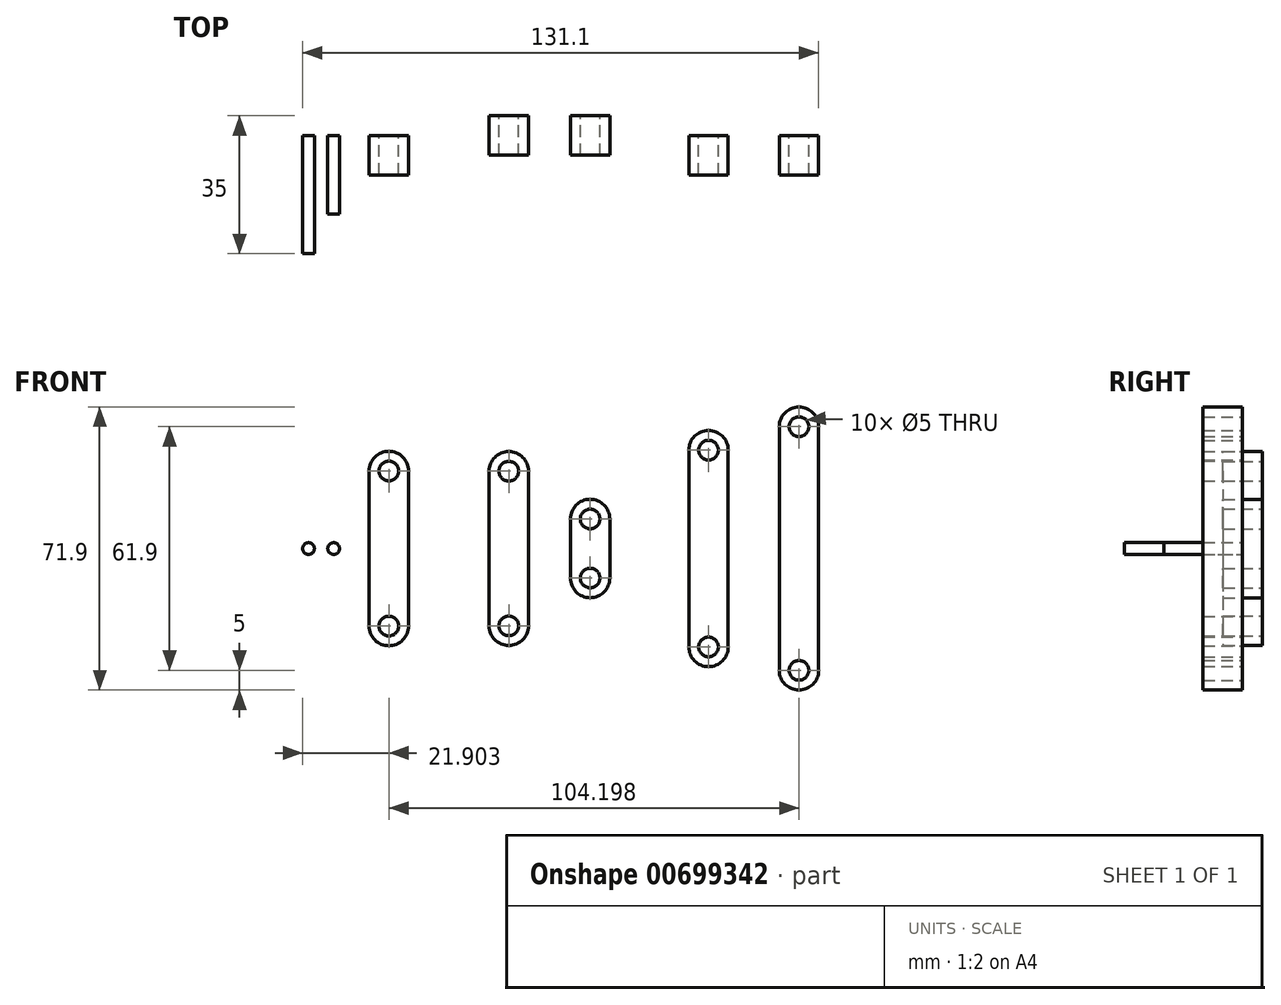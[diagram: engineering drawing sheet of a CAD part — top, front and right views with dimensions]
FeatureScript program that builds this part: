
annotation { "Feature Type Name" : "Feature", "Feature Type Description" : "" }
export const myFeature = defineFeature(function(context is Context, id is Id, definition is map)
    precondition{}
    {
        {
            assignVariable(context, id + "F0", {"name" : "thinkness", "anyValue" : 10});
        }
        {
            var Q0;
            Q0=qCreatedBy(makeId("Front.planeOp"),FACE);
            var sketch = newSketch(context, id + "F1", { "sketchPlane" : qUnion([Q0])});
            skCircle(sketch, "E0", {"center": v(0, 7.5) * mm, "radius": 2.5 * mm});
            skArc(sketch, "E1", {"start": v(5, 7.5) * mm, "mid": v(0, 12.5) * mm, "end": v(-5, 7.5) * mm});
            skLineSegment(sketch, "E2", {"start": v(-5, 7.5) * mm, "end": v(-5, 0) * mm});
            skLineSegment(sketch, "E3", {"start": v(-5, 0) * mm, "end": v(5, 0) * mm, "construction": true});
            skLineSegment(sketch, "E4", {"start": v(5, 0) * mm, "end": v(5, 7.5) * mm});
            skCircle(sketch, "E5.MirrorC", {"center": v(0, -7.5) * mm, "radius": 2.5 * mm});
            skArc(sketch, "E6.MirrorCS", {"start": v(5, -7.5) * mm, "mid": v(0, -12.5) * mm, "end": v(-5, -7.5) * mm});
            skLineSegment(sketch, "E7.MirrorCS", {"start": v(5, 0) * mm, "end": v(5, -7.5) * mm});
            skLineSegment(sketch, "E8.MirrorCS", {"start": v(-5, -7.5) * mm, "end": v(-5, 0) * mm});
            skSolve(sketch);
        }
        {
            var Q0;
            Q0 = qSketchRegion(id + "F1", true);
            extrude(context, id + "F2", {"entities" : qUnion([Q0]), "depth" : (getVariable(context, 'thinkness')) * mm, "offsetDistance" : 25 * mm, "symmetric" : true});
        }
        {
            var Q0;
            Q0=qCreatedBy(makeId("Front.planeOp"),FACE);
            var sketch = newSketch(context, id + "F3", { "sketchPlane" : qUnion([Q0])});
            skCircle(sketch, "E9", {"center": v(-20.66, 19.65) * mm, "radius": 2.5 * mm});
            skArc(sketch, "E10", {"start": v(-15.66, 19.65) * mm, "mid": v(-20.66, 24.65) * mm, "end": v(-25.66, 19.65) * mm});
            skLineSegment(sketch, "E11", {"start": v(-25.66, 19.65) * mm, "end": v(-25.66, 0) * mm});
            skLineSegment(sketch, "E12", {"start": v(-25.66, 0) * mm, "end": v(-15.66, 0) * mm, "construction": true});
            skLineSegment(sketch, "E13", {"start": v(-15.66, 0) * mm, "end": v(-15.66, 19.65) * mm});
            skCircle(sketch, "E14.MirrorC", {"center": v(-20.66, -19.65) * mm, "radius": 2.5 * mm});
            skArc(sketch, "E15.MirrorCS", {"start": v(-15.66, -19.65) * mm, "mid": v(-20.66, -24.65) * mm, "end": v(-25.66, -19.65) * mm});
            skLineSegment(sketch, "E16.MirrorCS", {"start": v(-15.66, 0) * mm, "end": v(-15.66, -19.65) * mm});
            skLineSegment(sketch, "E17.MirrorCS", {"start": v(-25.66, -19.65) * mm, "end": v(-25.66, 0) * mm});
            skSolve(sketch);
        }
        {
            var Q0;
            Q0 = qSketchRegion(id + "F3", true);
            extrude(context, id + "F4", {"entities" : qUnion([Q0]), "depth" : (getVariable(context, 'thinkness')) * mm, "offsetDistance" : 25 * mm, "symmetric" : true});
        }
        {
            var Q0;
            Q0=qCreatedBy(makeId("Front.planeOp"),FACE);
            var sketch = newSketch(context, id + "F5", { "sketchPlane" : qUnion([Q0])});
            skCircle(sketch, "E18", {"center": v(-51.14, 19.7) * mm, "radius": 2.5 * mm});
            skArc(sketch, "E19", {"start": v(-46.14, 19.7) * mm, "mid": v(-51.14, 24.7) * mm, "end": v(-56.14, 19.7) * mm});
            skLineSegment(sketch, "E20", {"start": v(-56.14, 19.7) * mm, "end": v(-56.14, 0) * mm});
            skLineSegment(sketch, "E21", {"start": v(-56.14, 0) * mm, "end": v(-46.14, 0) * mm, "construction": true});
            skLineSegment(sketch, "E22", {"start": v(-46.14, 0) * mm, "end": v(-46.14, 19.7) * mm});
            skCircle(sketch, "E23.MirrorC", {"center": v(-51.14, -19.7) * mm, "radius": 2.5 * mm});
            skArc(sketch, "E24.MirrorCS", {"start": v(-46.14, -19.7) * mm, "mid": v(-51.14, -24.7) * mm, "end": v(-56.14, -19.7) * mm});
            skLineSegment(sketch, "E25.MirrorCS", {"start": v(-46.14, 0) * mm, "end": v(-46.14, -19.7) * mm});
            skLineSegment(sketch, "E26.MirrorCS", {"start": v(-56.14, -19.7) * mm, "end": v(-56.14, 0) * mm});
            skSolve(sketch);
        }
        {
            var Q0;
            Q0 = qSketchRegion(id + "F5", true);
            extrude(context, id + "F6", {"entities" : qUnion([Q0]), "depth" : (getVariable(context, 'thinkness')) * mm, "offsetDistance" : 25 * mm});
        }
        {
            var Q0;
            Q0=qCreatedBy(makeId("Front.planeOp"),FACE);
            var sketch = newSketch(context, id + "F7", { "sketchPlane" : qUnion([Q0])});
            skCircle(sketch, "E27", {"center": v(30.08, 25) * mm, "radius": 2.5 * mm});
            skArc(sketch, "E28", {"start": v(35.08, 25) * mm, "mid": v(30.08, 30) * mm, "end": v(25.08, 25) * mm});
            skLineSegment(sketch, "E29", {"start": v(25.08, 25) * mm, "end": v(25.08, 0) * mm});
            skLineSegment(sketch, "E30", {"start": v(25.08, 0) * mm, "end": v(35.08, 0) * mm, "construction": true});
            skLineSegment(sketch, "E31", {"start": v(35.08, 0) * mm, "end": v(35.08, 25) * mm});
            skCircle(sketch, "E32.MirrorC", {"center": v(30.08, -25) * mm, "radius": 2.5 * mm});
            skArc(sketch, "E33.MirrorCS", {"start": v(35.08, -25) * mm, "mid": v(30.08, -30) * mm, "end": v(25.08, -25) * mm});
            skLineSegment(sketch, "E34.MirrorCS", {"start": v(35.08, 0) * mm, "end": v(35.08, -25) * mm});
            skLineSegment(sketch, "E35.MirrorCS", {"start": v(25.08, -25) * mm, "end": v(25.08, 0) * mm});
            skSolve(sketch);
        }
        {
            var Q0;
            Q0 = qSketchRegion(id + "F7", true);
            extrude(context, id + "F8", {"entities" : qUnion([Q0]), "depth" : (getVariable(context, 'thinkness')) * mm, "offsetDistance" : 25 * mm});
        }
        {
            var Q0;
            Q0=qCreatedBy(makeId("Front.planeOp"),FACE);
            var sketch = newSketch(context, id + "F9", { "sketchPlane" : qUnion([Q0])});
            skCircle(sketch, "E36", {"center": v(53.06, 30.95) * mm, "radius": 2.5 * mm});
            skArc(sketch, "E37", {"start": v(58.06, 30.95) * mm, "mid": v(53.06, 35.95) * mm, "end": v(48.06, 30.95) * mm});
            skLineSegment(sketch, "E38", {"start": v(48.06, 30.95) * mm, "end": v(48.06, 0) * mm});
            skLineSegment(sketch, "E39", {"start": v(48.06, 0) * mm, "end": v(58.06, 0) * mm, "construction": true});
            skLineSegment(sketch, "E40", {"start": v(58.06, 0) * mm, "end": v(58.06, 30.95) * mm});
            skCircle(sketch, "E41.MirrorC", {"center": v(53.06, -30.95) * mm, "radius": 2.5 * mm});
            skArc(sketch, "E42.MirrorCS", {"start": v(58.06, -30.95) * mm, "mid": v(53.06, -35.95) * mm, "end": v(48.06, -30.95) * mm});
            skLineSegment(sketch, "E43.MirrorCS", {"start": v(58.06, 0) * mm, "end": v(58.06, -30.95) * mm});
            skLineSegment(sketch, "E44.MirrorCS", {"start": v(48.06, -30.95) * mm, "end": v(48.06, 0) * mm});
            skSolve(sketch);
        }
        {
            var Q0;
            Q0 = qSketchRegion(id + "F9", true);
            extrude(context, id + "F10", {"entities" : qUnion([Q0]), "depth" : (getVariable(context, 'thinkness')) * mm, "offsetDistance" : 25 * mm});
        }
        {
            var Q0;
            Q0=qCreatedBy(makeId("Front.planeOp"),FACE);
            var sketch = newSketch(context, id + "F11", { "sketchPlane" : qUnion([Q0])});
            skCircle(sketch, "E45", {"center": v(-65.16, 0) * mm, "radius": 1.5 * mm});
            skSolve(sketch);
        }
        {
            var Q0;
            Q0 = qSketchRegion(id + "F11", true);
            extrude(context, id + "F12", {"entities" : qUnion([Q0]), "depth" : (getVariable(context, 'thinkness') * 2) * mm, "offsetDistance" : 25 * mm});
        }
        {
            var Q0;
            Q0=qCreatedBy(makeId("Front.planeOp"),FACE);
            var sketch = newSketch(context, id + "F13", { "sketchPlane" : qUnion([Q0])});
            skCircle(sketch, "E46", {"center": v(-71.54, 0) * mm, "radius": 1.5 * mm});
            skSolve(sketch);
        }
        {
            var Q0;
            Q0 = qSketchRegion(id + "F13", true);
            extrude(context, id + "F14", {"entities" : qUnion([Q0]), "depth" : (getVariable(context, 'thinkness') * 3) * mm, "offsetDistance" : 25 * mm});
        }
    });
